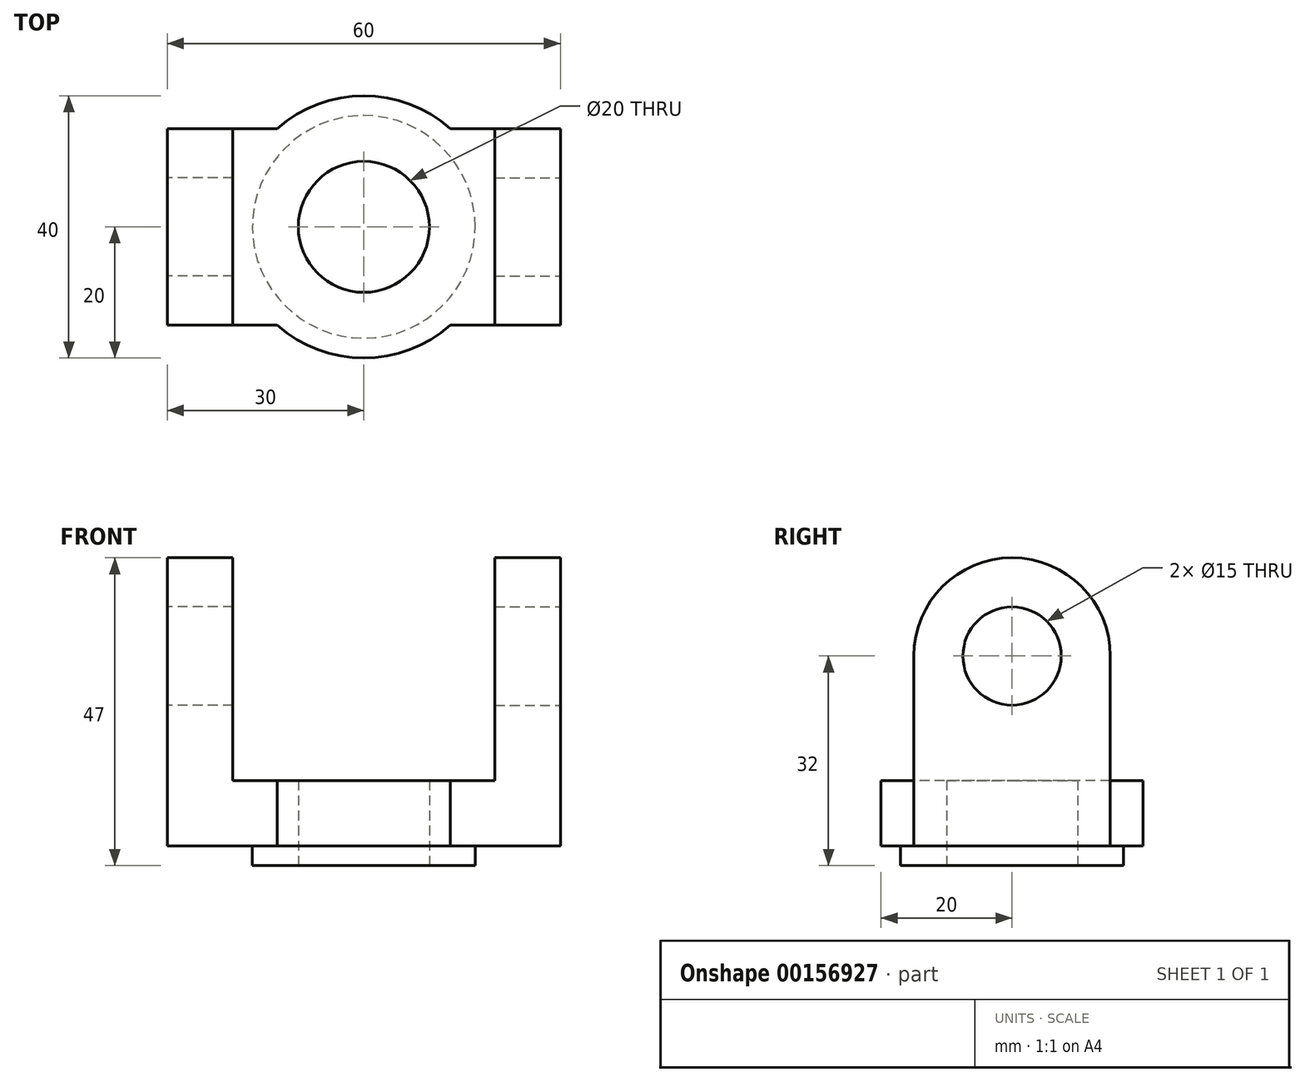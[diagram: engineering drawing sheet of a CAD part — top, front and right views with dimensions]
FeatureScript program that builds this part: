
annotation { "Feature Type Name" : "Feature", "Feature Type Description" : "" }
export const myFeature = defineFeature(function(context is Context, id is Id, definition is map)
    precondition{}
    {
        {
            var Q0;
            Q0=qCreatedBy(makeId("Top.planeOp"),FACE);
            var sketch = newSketch(context, id + "F0", { "sketchPlane" : qUnion([Q0])});
            skCircle(sketch, "E0", {"center": v(0, 0) * mm, "radius": 10 * mm});
            skLineSegment(sketch, "E1.bottom", {"start": v(-30, 15) * mm, "end": v(-13.23, 15) * mm});
            skLineSegment(sketch, "E1.top", {"start": v(-30, -15) * mm, "end": v(-13.23, -15) * mm});
            skLineSegment(sketch, "E1.left", {"start": v(-30, 15) * mm, "end": v(-30, -15) * mm});
            skLineSegment(sketch, "E1.right", {"start": v(30, 15) * mm, "end": v(30, -15) * mm});
            skArc(sketch, "E2", {"start": v(13.23, 15) * mm, "mid": v(0, 20) * mm, "end": v(-13.23, 15) * mm});
            skLineSegment(sketch, "E3", {"start": v(0, -15) * mm, "end": v(0, -15) * mm});
            skLineSegment(sketch, "E4.trimOffspring", {"start": v(13.23, 15) * mm, "end": v(30, 15) * mm});
            skLineSegment(sketch, "E5.trimOffspring", {"start": v(13.23, -15) * mm, "end": v(30, -15) * mm});
            skArc(sketch, "E6", {"start": v(-13.23, -15) * mm, "mid": v(0, -20) * mm, "end": v(13.23, -15) * mm});
            skSolve(sketch);
        }
        {
            var Q0;
            Q0 = qSketchRegion(id + "F0", true);
            extrude(context, id + "F1", {"entities" : qUnion([Q0]), "depth" : 10 * mm});
        }
        {
            var Q0;
            Q0=makeQuery(id+"F1.opExtrude","SWEPT_FACE",FACE,{"disambiguationData":[OSD([sQuery(id+"F0.wireOp",EDGE,"E1.right")])]});
            cPlane(context, id + "F2", {"entities" : qUnion([Q0]), "cplaneType" : CPlaneType.OFFSET, "offset" : 0 * mm, "width" : 150 * mm, "height" : 150 * mm});
        }
        {
            var Q0;
            Q0=qCreatedBy(id+"F2.planeOp",FACE);
            var sketch = newSketch(context, id + "F3", { "sketchPlane" : qUnion([Q0])});
            skLineSegment(sketch, "E7.bottom", {"start": v(-15, 0) * mm, "end": v(15, 0) * mm});
            skLineSegment(sketch, "E7.left", {"start": v(-15, 0) * mm, "end": v(-15, 29) * mm});
            skLineSegment(sketch, "E7.right", {"start": v(15, 0) * mm, "end": v(15, 29) * mm});
            skCircle(sketch, "E8", {"center": v(0, 29) * mm, "radius": 7.5 * mm});
            skArc(sketch, "E9", {"start": v(-15, 29) * mm, "mid": v(0, 44) * mm, "end": v(15, 29) * mm});
            skSolve(sketch);
        }
        {
            var Q0;
            Q0=qCreatedBy(makeId("Top.planeOp"),FACE);
            var sketch = newSketch(context, id + "F4", { "sketchPlane" : qUnion([Q0])});
            skCircle(sketch, "E10", {"center": v(0, 0) * mm, "radius": 17 * mm});
            skCircle(sketch, "E11", {"center": v(0, 0) * mm, "radius": 10 * mm});
            skSolve(sketch);
        }
        {
            var Q0;
            Q0 = qSketchRegion(id + "F4", true);
            extrude(context, id + "F5", {"entities" : qUnion([Q0]), "operationType" : NewBodyOperationType.ADD, "oppositeDirection" : true, "depth" : 3 * mm});
        }
        {
            var Q0;
            Q0 = qSketchRegion(id + "F3", true);
            extrude(context, id + "F6", {"entities" : qUnion([Q0]), "operationType" : NewBodyOperationType.ADD, "oppositeDirection" : true, "depth" : 10 * mm});
        }
        {
            var Q0;
            Q0=makeQuery(id+"F1.opExtrude","SWEPT_FACE",FACE,{"disambiguationData":[OSD([sQuery(id+"F0.wireOp",EDGE,"E1.left")])]});
            var sketch = newSketch(context, id + "F7", { "sketchPlane" : qUnion([Q0])});
            skLineSegment(sketch, "E12", {"start": v(-15, 0) * mm, "end": v(-15, 29) * mm});
            skLineSegment(sketch, "E13", {"start": v(-15, 0) * mm, "end": v(15, 0) * mm});
            skLineSegment(sketch, "E14", {"start": v(15, 0) * mm, "end": v(15, 29) * mm});
            skCircle(sketch, "E15", {"center": v(0, 29) * mm, "radius": 7.5 * mm});
            skArc(sketch, "E16", {"start": v(15, 29) * mm, "mid": v(0, 44) * mm, "end": v(-15, 29) * mm});
            skSolve(sketch);
        }
        {
            var Q0;
            Q0 = qSketchRegion(id + "F7", true);
            extrude(context, id + "F8", {"entities" : qUnion([Q0]), "operationType" : NewBodyOperationType.ADD, "oppositeDirection" : true, "depth" : 10 * mm});
        }
    });
